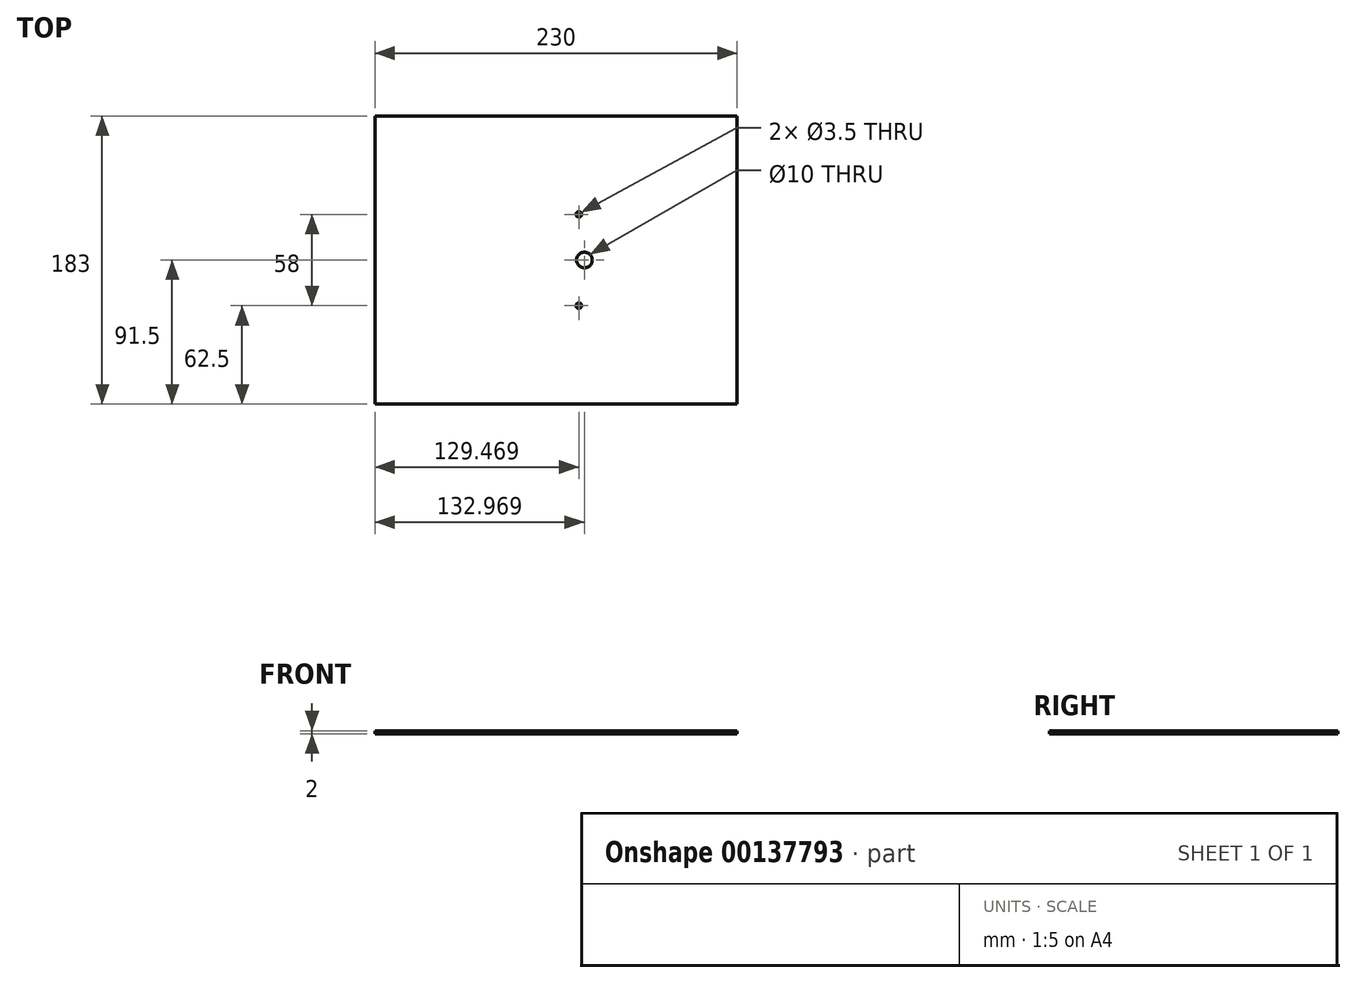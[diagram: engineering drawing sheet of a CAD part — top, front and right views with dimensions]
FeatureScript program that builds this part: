
annotation { "Feature Type Name" : "Feature", "Feature Type Description" : "" }
export const myFeature = defineFeature(function(context is Context, id is Id, definition is map)
    precondition{}
    {
        {
            var Q0;
            Q0=qCreatedBy(makeId("Top.planeOp"),FACE);
            var sketch = newSketch(context, id + "F0", { "sketchPlane" : qUnion([Q0])});
            skLineSegment(sketch, "E0.bottom", {"start": v(115, 91.5) * mm, "end": v(-115, 91.5) * mm});
            skLineSegment(sketch, "E0.top", {"start": v(115, -91.5) * mm, "end": v(-115, -91.5) * mm});
            skLineSegment(sketch, "E0.left", {"start": v(115, 91.5) * mm, "end": v(115, -91.5) * mm});
            skLineSegment(sketch, "E0.right", {"start": v(-115, 91.5) * mm, "end": v(-115, -91.5) * mm});
            skPoint(sketch, "E0.middle", {"position": v(0, 0) * mm});
            skSolve(sketch);
        }
        {
            var Q0;
            Q0 = qSketchRegion(id + "F0", true);
            extrude(context, id + "F1", {"entities" : qUnion([Q0]), "depth" : 2 * mm});
        }
        {
            var Q0;
            Q0=makeQuery(id+"F1.opExtrude","CAP_FACE",FACE,{"disambiguationData":[OSD([sQuery(id+"F0.wireOp",EDGE,"E0.bottom"),sQuery(id+"F0.wireOp",EDGE,"E0.top"),sQuery(id+"F0.wireOp",EDGE,"E0.left"),sQuery(id+"F0.wireOp",EDGE,"E0.right")])],"isStart":false});
            var sketch = newSketch(context, id + "F2", { "sketchPlane" : qUnion([Q0])});
            skCircle(sketch, "E1", {"center": v(17.97, 0) * mm, "radius": 5 * mm});
            skSolve(sketch);
        }
        {
            var Q0;
            Q0 = qSketchRegion(id + "F2", true);
            extrude(context, id + "F3", {"entities" : qUnion([Q0]), "operationType" : NewBodyOperationType.REMOVE, "endBound" : BoundingType.THROUGH_ALL, "oppositeDirection" : true, "depth" : 25 * mm});
        }
        {
            var Q0;
            Q0=makeQuery(id+"F1.opExtrude","CAP_FACE",FACE,{"disambiguationData":[OSD([sQuery(id+"F0.wireOp",EDGE,"E0.bottom"),sQuery(id+"F0.wireOp",EDGE,"E0.top"),sQuery(id+"F0.wireOp",EDGE,"E0.left"),sQuery(id+"F0.wireOp",EDGE,"E0.right")])],"isStart":false});
            var sketch = newSketch(context, id + "F4", { "sketchPlane" : qUnion([Q0])});
            skLineSegment(sketch, "E2", {"start": v(17.97, 0) * mm, "end": v(14.47, 0) * mm, "construction": true});
            skLineSegment(sketch, "E3", {"start": v(14.47, 0) * mm, "end": v(14.47, 29) * mm, "construction": true});
            skCircle(sketch, "E4", {"center": v(14.47, 29) * mm, "radius": 1.75 * mm});
            skLineSegment(sketch, "E5", {"start": v(14.47, 0) * mm, "end": v(14.47, -29) * mm, "construction": true});
            skCircle(sketch, "E6", {"center": v(14.47, -29) * mm, "radius": 1.75 * mm});
            skSolve(sketch);
        }
        {
            var Q0;
            Q0 = qSketchRegion(id + "F4", true);
            extrude(context, id + "F5", {"entities" : qUnion([Q0]), "operationType" : NewBodyOperationType.REMOVE, "endBound" : BoundingType.THROUGH_ALL, "oppositeDirection" : true, "depth" : 25 * mm});
        }
    });
